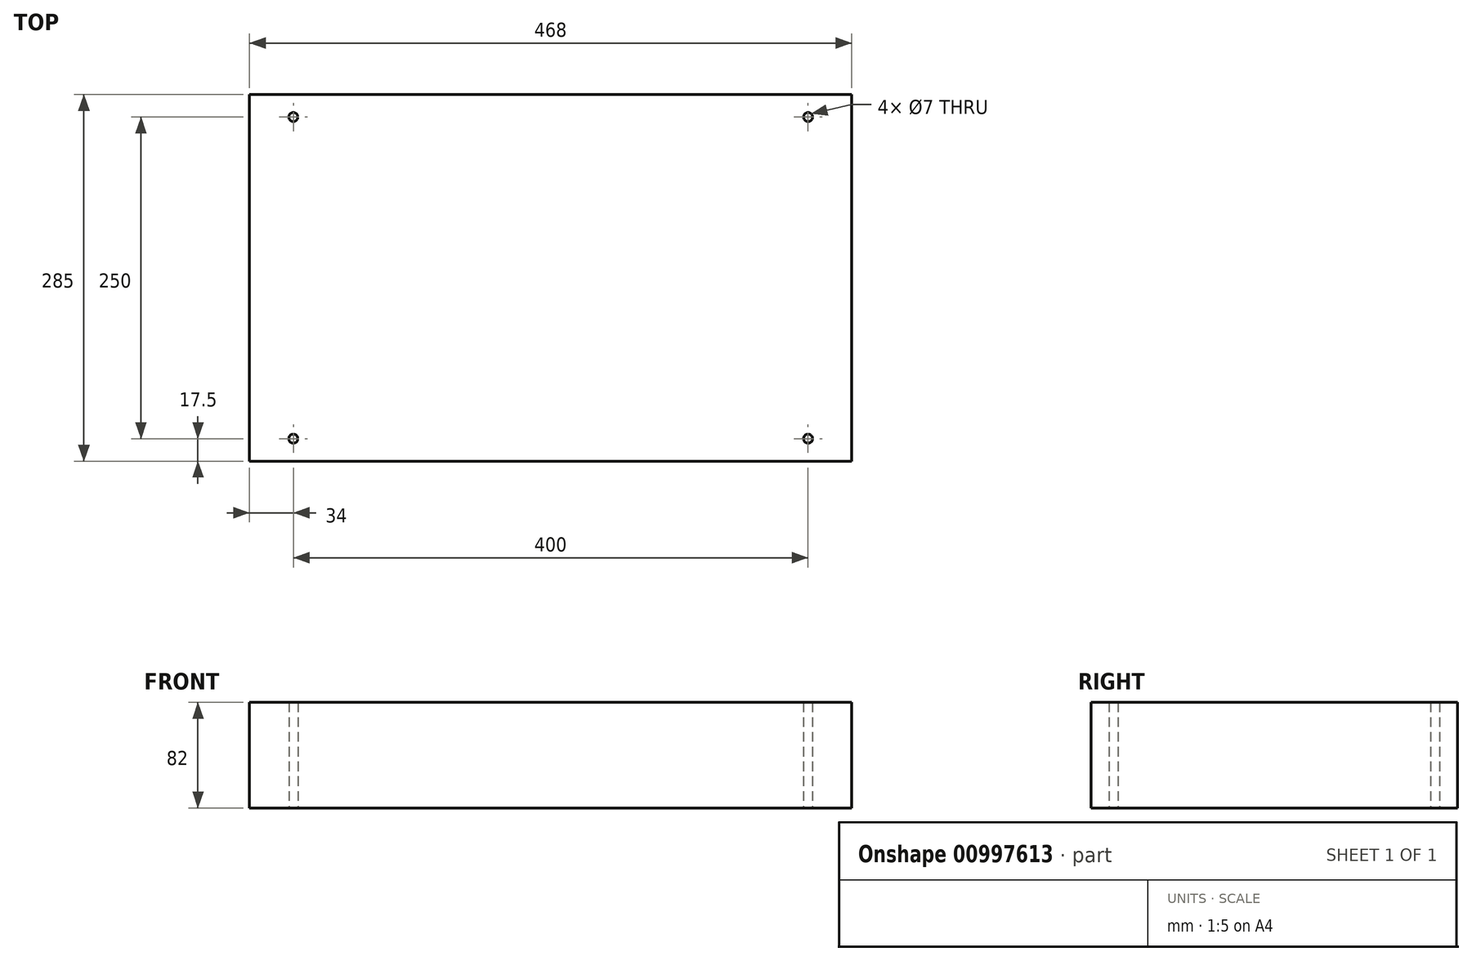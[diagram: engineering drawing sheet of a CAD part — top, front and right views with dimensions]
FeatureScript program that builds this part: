
annotation { "Feature Type Name" : "Feature", "Feature Type Description" : "" }
export const myFeature = defineFeature(function(context is Context, id is Id, definition is map)
    precondition{}
    {
        {
            var Q0;
            Q0=qCreatedBy(makeId("Top.planeOp"),FACE);
            var sketch = newSketch(context, id + "F0", { "sketchPlane" : qUnion([Q0])});
            skLineSegment(sketch, "E0.bottom", {"start": v(234, -142.5) * mm, "end": v(-234, -142.5) * mm});
            skLineSegment(sketch, "E0.top", {"start": v(234, 142.5) * mm, "end": v(-234, 142.5) * mm});
            skLineSegment(sketch, "E0.left", {"start": v(234, -142.5) * mm, "end": v(234, 142.5) * mm});
            skLineSegment(sketch, "E0.right", {"start": v(-234, -142.5) * mm, "end": v(-234, 142.5) * mm});
            skPoint(sketch, "E0.middle", {"position": v(0, 0) * mm});
            skCircle(sketch, "E1", {"center": v(-200, -125) * mm, "radius": 3.5 * mm});
            skCircle(sketch, "E2.MirrorC", {"center": v(200, -125) * mm, "radius": 3.5 * mm});
            skCircle(sketch, "E3.MirrorC", {"center": v(-200, 125) * mm, "radius": 3.5 * mm});
            skCircle(sketch, "E4.MirrorC", {"center": v(200, 125) * mm, "radius": 3.5 * mm});
            skSolve(sketch);
        }
        {
            var Q0;
            Q0=makeQuery(id+"F0.imprint","IMPRINT",FACE,{"disambiguationData":[TD([[makeQuery(id+"F0.imprint","IMPRINT",EDGE,{"derivedFrom":sQuery(id+"F0.wireOp",EDGE,"E0.bottom")}),-1.0]])]});
            extrude(context, id + "F1", {"entities" : qUnion([Q0]), "depth" : 82 * mm, "offsetDistance" : 25 * mm});
        }
    });
